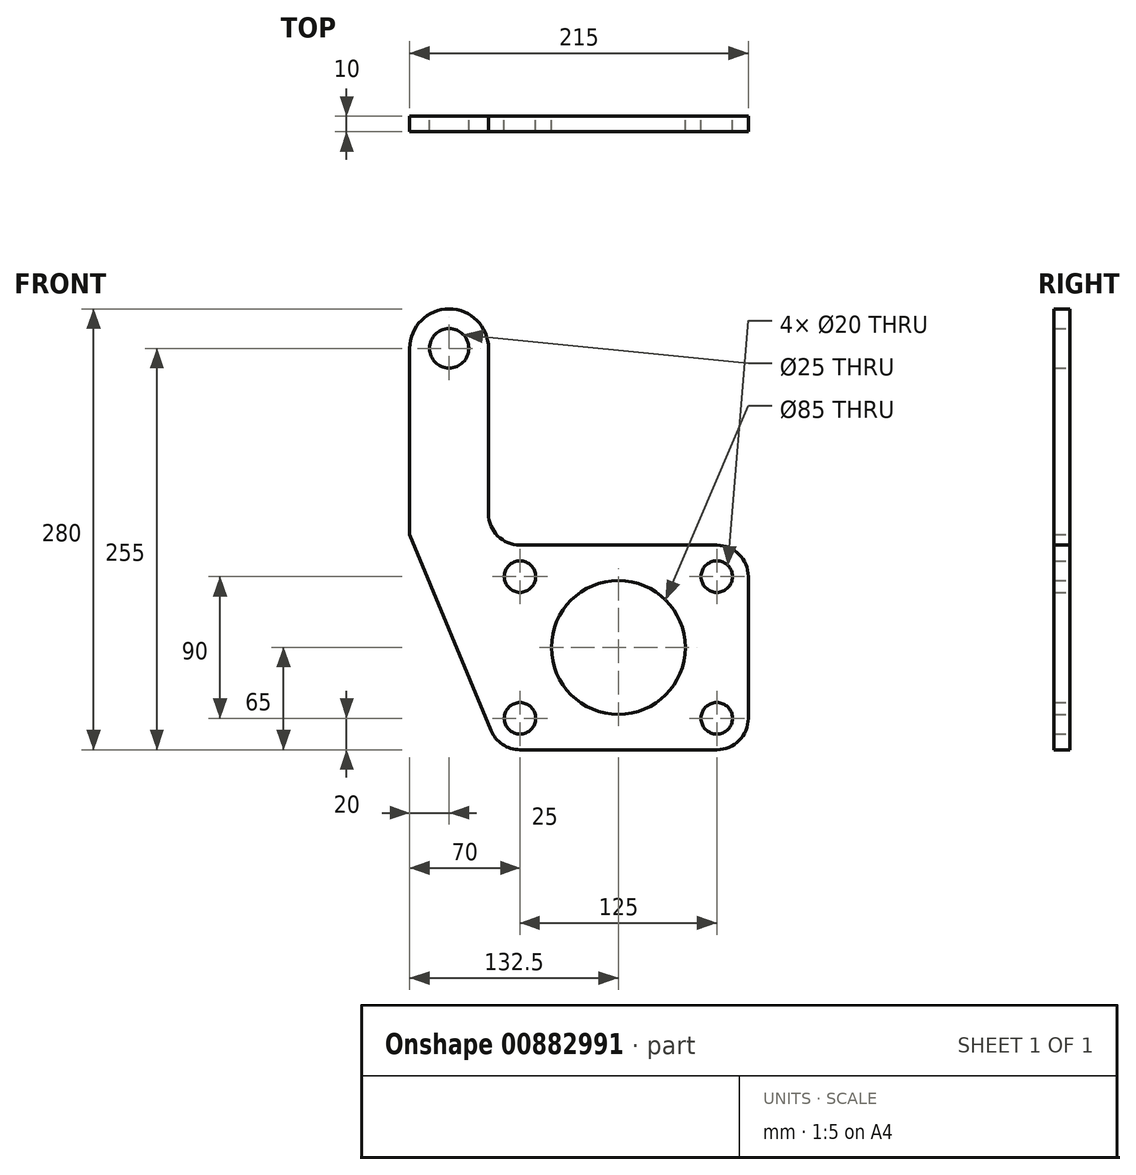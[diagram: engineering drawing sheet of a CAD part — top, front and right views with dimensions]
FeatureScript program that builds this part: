
annotation { "Feature Type Name" : "Feature", "Feature Type Description" : "" }
export const myFeature = defineFeature(function(context is Context, id is Id, definition is map)
    precondition{}
    {
        {
            var Q0;
            Q0=qCreatedBy(makeId("Front.planeOp"),FACE);
            var sketch = newSketch(context, id + "F0", { "sketchPlane" : qUnion([Q0])});
            skCircle(sketch, "E0", {"center": v(0, 0) * mm, "radius": 10 * mm});
            skCircle(sketch, "E1", {"center": v(0, -90) * mm, "radius": 10 * mm});
            skCircle(sketch, "E2", {"center": v(-125, -90) * mm, "radius": 10 * mm});
            skCircle(sketch, "E3", {"center": v(-125, 0) * mm, "radius": 10 * mm});
            skArc(sketch, "E4", {"start": v(0, 20) * mm, "mid": v(14.14, 14.14) * mm, "end": v(20, 0) * mm});
            skArc(sketch, "E5", {"start": v(20, -90) * mm, "mid": v(14.14, -104.14) * mm, "end": v(0, -110) * mm});
            skLineSegment(sketch, "E6", {"start": v(20, 0) * mm, "end": v(20, -90) * mm});
            skLineSegment(sketch, "E7", {"start": v(0, 20) * mm, "end": v(-125, 20) * mm});
            skLineSegment(sketch, "E8", {"start": v(0, -110) * mm, "end": v(-125, -110) * mm});
            skCircle(sketch, "E9", {"center": v(-170, 145) * mm, "radius": 12.5 * mm});
            skArc(sketch, "E10", {"start": v(-195, 145) * mm, "mid": v(-170, 170) * mm, "end": v(-145, 145) * mm});
            skLineSegment(sketch, "E11", {"start": v(-195, 145) * mm, "end": v(-195, 26.73) * mm});
            skLineSegment(sketch, "E12", {"start": v(-145, 145) * mm, "end": v(-145, 40) * mm});
            skArc(sketch, "E13", {"start": v(-125, -110) * mm, "mid": v(-136.11, -106.63) * mm, "end": v(-143.48, -97.65) * mm});
            skArc(sketch, "E14.filletArc", {"start": v(-145, 40) * mm, "mid": v(-139.14, 25.86) * mm, "end": v(-125, 20) * mm});
            skLineSegment(sketch, "E15", {"start": v(-195, 26.73) * mm, "end": v(-142.8, -99.3) * mm});
            skPoint(sketch, "E15.endSnap0", {"position": v(-142.8, -99.12) * mm});
            skLineSegment(sketch, "E16", {"start": v(-125, 0) * mm, "end": v(0, -90) * mm, "construction": true});
            skLineSegment(sketch, "E17", {"start": v(0, 0) * mm, "end": v(-125, -90) * mm, "construction": true});
            skCircle(sketch, "E18", {"center": v(-62.5, -45) * mm, "radius": 42.5 * mm});
            skSolve(sketch);
        }
        {
            var Q0;
            Q0=makeQuery(id+"F0.imprint","IMPRINT",FACE,{"disambiguationData":[TD([[makeQuery(id+"F0.imprint","IMPRINT",EDGE,{"derivedFrom":sQuery(id+"F0.wireOp",EDGE,"E0")}),-1.0]])]});
            extrude(context, id + "F1", {"entities" : qUnion([Q0]), "depth" : 10 * mm, "offsetDistance" : 25 * mm});
        }
    });
